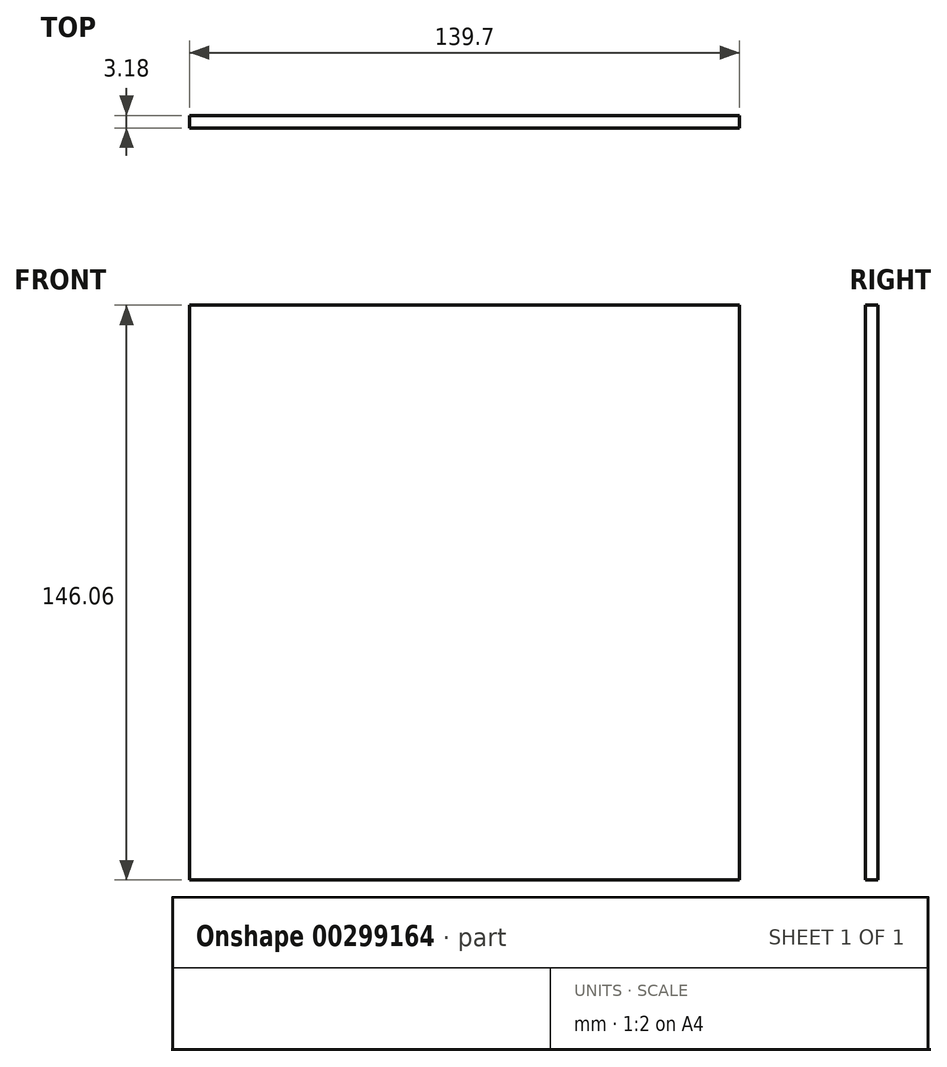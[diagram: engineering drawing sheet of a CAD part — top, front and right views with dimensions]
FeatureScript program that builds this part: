
annotation { "Feature Type Name" : "Feature", "Feature Type Description" : "" }
export const myFeature = defineFeature(function(context is Context, id is Id, definition is map)
    precondition{}
    {
        {
            var Q0;
            Q0=qCreatedBy(makeId("Front.planeOp"),FACE);
            var sketch = newSketch(context, id + "F0", { "sketchPlane" : qUnion([Q0])});
            skLineSegment(sketch, "E0.bottom", {"start": v(-69.85, 73.03) * mm, "end": v(69.85, 73.03) * mm});
            skLineSegment(sketch, "E0.top", {"start": v(-69.85, -73.03) * mm, "end": v(69.85, -73.03) * mm});
            skLineSegment(sketch, "E0.left", {"start": v(-69.85, 73.03) * mm, "end": v(-69.85, -73.03) * mm});
            skLineSegment(sketch, "E0.right", {"start": v(69.85, 73.03) * mm, "end": v(69.85, -73.03) * mm});
            skPoint(sketch, "E0.middle", {"position": v(0, 0) * mm});
            skSolve(sketch);
        }
        {
            var Q0;
            Q0 = qSketchRegion(id + "F0", true);
            extrude(context, id + "F1", {"entities" : qUnion([Q0]), "endBound" : BoundingType.SYMMETRIC, "depth" : 3.17 * mm});
        }
    });
